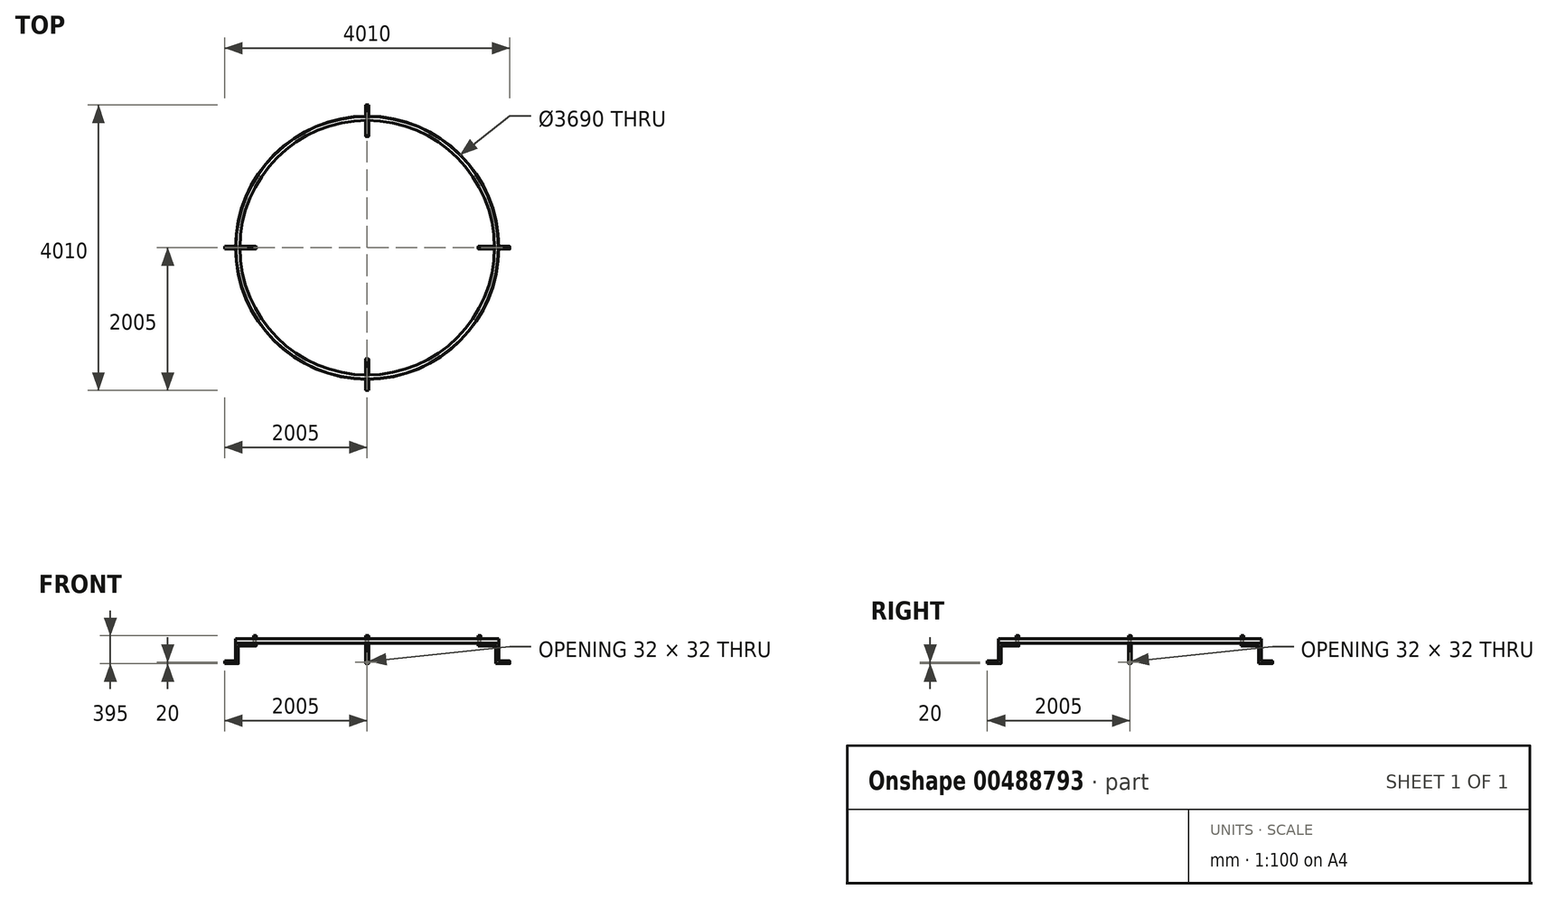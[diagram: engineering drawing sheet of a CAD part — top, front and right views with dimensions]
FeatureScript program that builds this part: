
annotation { "Feature Type Name" : "Feature", "Feature Type Description" : "" }
export const myFeature = defineFeature(function(context is Context, id is Id, definition is map)
    precondition{}
    {
        {
            var Q0;
            Q0=qCreatedBy(makeId("Front.planeOp"),FACE);
            var sketch = newSketch(context, id + "F0", { "sketchPlane" : qUnion([Q0])});
            skLineSegment(sketch, "E0", {"start": v(0, 0) * mm, "end": v(0, 129.65) * mm, "construction": true});
            skLineSegment(sketch, "E1", {"start": v(1790, 0) * mm, "end": v(1850, 0) * mm});
            skLineSegment(sketch, "E2", {"start": v(1850, 0) * mm, "end": v(1850, 60) * mm});
            skLineSegment(sketch, "E3.0", {"start": v(1845, 10) * mm, "end": v(1845, 55) * mm});
            skLineSegment(sketch, "E3.1", {"start": v(1795, 5) * mm, "end": v(1840, 5) * mm});
            skLineSegment(sketch, "E4", {"start": v(1850, 60) * mm, "end": v(1850, 60) * mm});
            skLineSegment(sketch, "E5", {"start": v(1790, 0) * mm, "end": v(1790, 0) * mm});
            skPoint(sketch, "E6.visualSharp", {"position": v(1845, 5) * mm});
            skArc(sketch, "E6.filletArc", {"start": v(1840, 5) * mm, "mid": v(1843.54, 6.46) * mm, "end": v(1845, 10) * mm});
            skPoint(sketch, "E7.visualSharp", {"position": v(1845, 60) * mm});
            skArc(sketch, "E7.filletArc", {"start": v(1850, 60) * mm, "mid": v(1846.46, 58.54) * mm, "end": v(1845, 55) * mm});
            skPoint(sketch, "E8.visualSharp", {"position": v(1790, 5) * mm});
            skArc(sketch, "E8.filletArc", {"start": v(1795, 5) * mm, "mid": v(1791.46, 3.54) * mm, "end": v(1790, 0) * mm});
            skSolve(sketch);
        }
        {
            var Q0;
            Q0=makeQuery(id+"F0.imprint","IMPRINT",FACE,{"disambiguationData":[TD([[makeQuery(id+"F0.imprint","IMPRINT",EDGE,{"derivedFrom":sQuery(id+"F0.wireOp",EDGE,"E1")}),1.0]])]});
            var Q1;
            Q1=sQuery(id+"F0.wireOp",EDGE,"E0");
            revolve(context, id + "F1", {"entities" : qUnion([Q0]), "axis" : qUnion([Q1]), "revolveType" : RevolveType.FULL});
        }
        {
            var Q0;
            Q0=qCreatedBy(makeId("Right.planeOp"),FACE);
            var sketch = newSketch(context, id + "F2", { "sketchPlane" : qUnion([Q0])});
            skLineSegment(sketch, "E9", {"start": v(-2005, -270) * mm, "end": v(-1830, -270) * mm});
            skLineSegment(sketch, "E10", {"start": v(-1830, -270) * mm, "end": v(-1830, -20) * mm});
            skLineSegment(sketch, "E11", {"start": v(-1830, -20) * mm, "end": v(-1580, -20) * mm});
            skLineSegment(sketch, "E12", {"start": v(-1580, -20) * mm, "end": v(-1580, 105) * mm});
            skSolve(sketch);
        }
        {
            var Q0;
            Q0=qCreatedBy(makeId("Front.planeOp"),FACE);
            var Q1;
            Q1=sQuery(id+"F2.wireOp",VERTEX,"E9.start");
            cPlane(context, id + "F3", {"entities" : qUnion([Q0, Q1]), "cplaneType" : CPlaneType.PLANE_POINT, "offset" : 25 * mm, "width" : 150 * mm, "height" : 150 * mm});
        }
        {
            var Q0;
            Q0=qCreatedBy(id+"F3.planeOp",FACE);
            var sketch = newSketch(context, id + "F4", { "sketchPlane" : qUnion([Q0])});
            skLineSegment(sketch, "E13.bottom", {"start": v(12, -290) * mm, "end": v(-12, -290) * mm});
            skLineSegment(sketch, "E13.top", {"start": v(12, -250) * mm, "end": v(-12, -250) * mm});
            skLineSegment(sketch, "E13.left", {"start": v(20, -282) * mm, "end": v(20, -258) * mm});
            skLineSegment(sketch, "E13.right", {"start": v(-20, -282) * mm, "end": v(-20, -258) * mm});
            skPoint(sketch, "E13.middle", {"position": v(0, -270) * mm});
            skPoint(sketch, "E14.visualSharp", {"position": v(-20, -250) * mm});
            skArc(sketch, "E14.filletArc", {"start": v(-12, -250) * mm, "mid": v(-17.66, -252.34) * mm, "end": v(-20, -258) * mm});
            skPoint(sketch, "E15.visualSharp", {"position": v(20, -250) * mm});
            skArc(sketch, "E15.filletArc", {"start": v(20, -258) * mm, "mid": v(17.66, -252.34) * mm, "end": v(12, -250) * mm});
            skPoint(sketch, "E16.visualSharp", {"position": v(20, -290) * mm});
            skArc(sketch, "E16.filletArc", {"start": v(12, -290) * mm, "mid": v(17.66, -287.66) * mm, "end": v(20, -282) * mm});
            skPoint(sketch, "E17.visualSharp", {"position": v(-20, -290) * mm});
            skArc(sketch, "E17.filletArc", {"start": v(-20, -282) * mm, "mid": v(-17.66, -287.66) * mm, "end": v(-12, -290) * mm});
            skArc(sketch, "E18.0", {"start": v(16, -258) * mm, "mid": v(14.83, -255.17) * mm, "end": v(12, -254) * mm});
            skLineSegment(sketch, "E18.1", {"start": v(16, -282) * mm, "end": v(16, -258) * mm});
            skLineSegment(sketch, "E18.2", {"start": v(12, -254) * mm, "end": v(-12, -254) * mm});
            skArc(sketch, "E18.3", {"start": v(12, -286) * mm, "mid": v(14.83, -284.83) * mm, "end": v(16, -282) * mm});
            skArc(sketch, "E18.4", {"start": v(-12, -254) * mm, "mid": v(-14.83, -255.17) * mm, "end": v(-16, -258) * mm});
            skLineSegment(sketch, "E18.5", {"start": v(-16, -282) * mm, "end": v(-16, -258) * mm});
            skArc(sketch, "E18.6", {"start": v(-16, -282) * mm, "mid": v(-14.83, -284.83) * mm, "end": v(-12, -286) * mm});
            skLineSegment(sketch, "E18.7", {"start": v(12, -286) * mm, "end": v(-12, -286) * mm});
            skSolve(sketch);
        }
        {
            var Q0;
            Q0=makeQuery(id+"F4.imprint","IMPRINT",FACE,{"disambiguationData":[TD([[makeQuery(id+"F4.imprint","IMPRINT",EDGE,{"derivedFrom":sQuery(id+"F4.wireOp",EDGE,"E13.bottom")}),-1.0]])]});
            var Q1;
            Q1=sQuery(id+"F2.wireOp",EDGE,"E9");
            var Q2;
            Q2=sQuery(id+"F2.wireOp",EDGE,"E10");
            var Q3;
            Q3=sQuery(id+"F2.wireOp",EDGE,"E11");
            var Q4;
            Q4=sQuery(id+"F2.wireOp",EDGE,"E12");
            sweep(context, id + "F5", {"profiles" : qUnion([Q0]), "path" : qUnion([Q1, Q2, Q3, Q4])});
        }
        {
            var Q0;
            Q0=makeQuery(id+"F5.opSweep","SWEPT_BODY",BODY,{"disambiguationData":[OSD([sQuery(id+"F2.wireOp",EDGE,"E12"),sQuery(id+"F4.wireOp",EDGE,"E13.bottom"),sQuery(id+"F4.wireOp",EDGE,"E13.top"),sQuery(id+"F4.wireOp",EDGE,"E13.left"),sQuery(id+"F4.wireOp",EDGE,"E13.right"),sQuery(id+"F4.wireOp",EDGE,"E14.filletArc"),sQuery(id+"F4.wireOp",EDGE,"E15.filletArc"),sQuery(id+"F4.wireOp",EDGE,"E16.filletArc"),sQuery(id+"F4.wireOp",EDGE,"E17.filletArc"),sQuery(id+"F4.wireOp",EDGE,"E18.0"),sQuery(id+"F4.wireOp",EDGE,"E18.1"),sQuery(id+"F4.wireOp",EDGE,"E18.2"),sQuery(id+"F4.wireOp",EDGE,"E18.3"),sQuery(id+"F4.wireOp",EDGE,"E18.4"),sQuery(id+"F4.wireOp",EDGE,"E18.5"),sQuery(id+"F4.wireOp",EDGE,"E18.6"),sQuery(id+"F4.wireOp",EDGE,"E18.7")])]});
            var Q1;
            Q1=makeQuery(id+"F1.opRevolve","SWEPT_EDGE",EDGE,{"disambiguationData":[OSD([sQuery(id+"F0.wireOp",EDGE,"E2"),sQuery(id+"F0.wireOp",EDGE,"E7.filletArc")])]});
            circularPattern(context, id + "F6", {"entities" : qUnion([Q0]), "axis" : qUnion([Q1]), "angle" : 360 * degree, "instanceCount" : 4, "equalSpace" : true});
        }
    });
